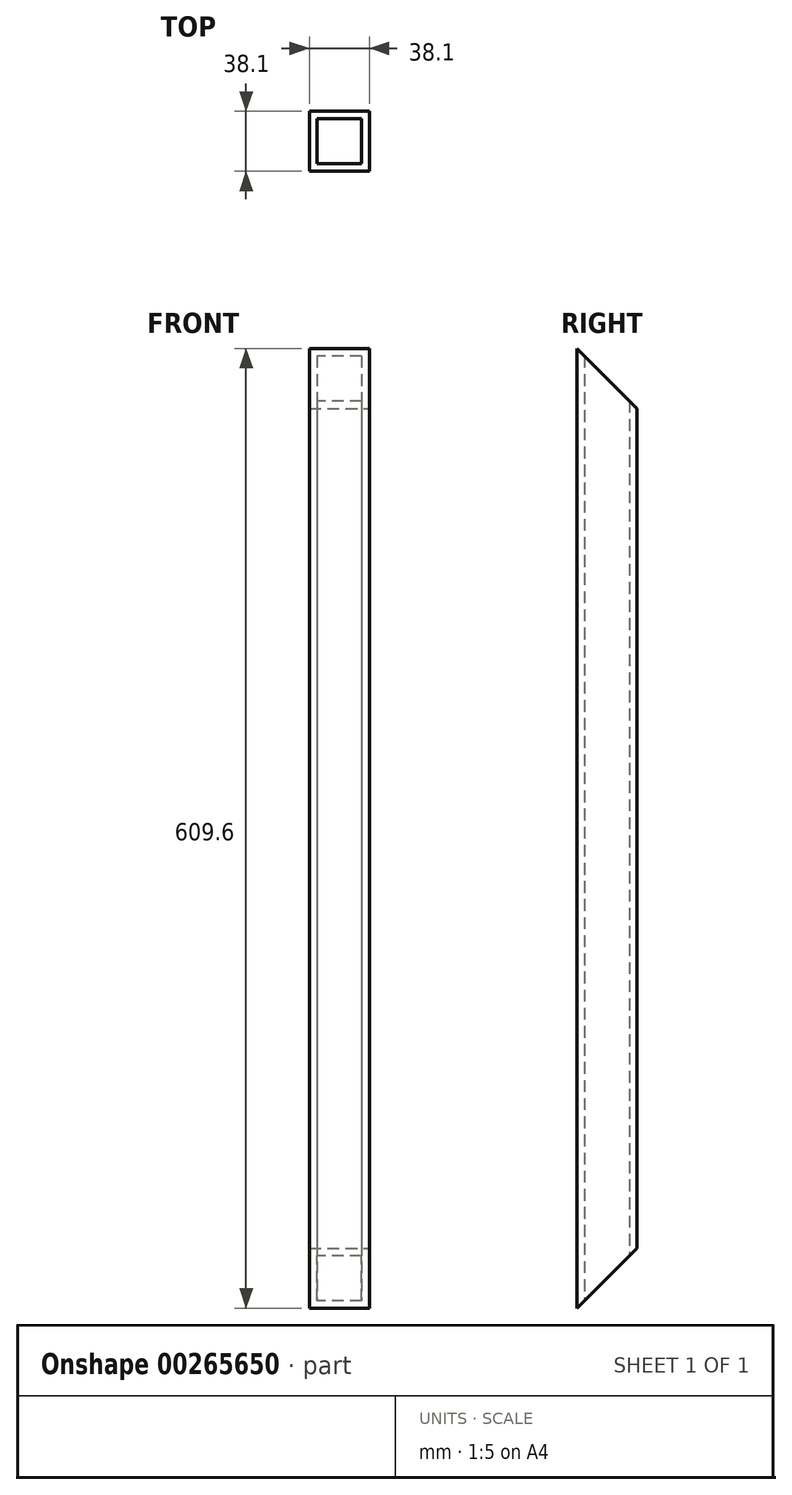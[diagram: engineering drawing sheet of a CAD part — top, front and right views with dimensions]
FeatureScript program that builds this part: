
annotation { "Feature Type Name" : "Feature", "Feature Type Description" : "" }
export const myFeature = defineFeature(function(context is Context, id is Id, definition is map)
    precondition{}
    {
        {
            var Q0;
            Q0=qCreatedBy(makeId("Top.planeOp"),FACE);
            var sketch = newSketch(context, id + "F0", { "sketchPlane" : qUnion([Q0])});
            skLineSegment(sketch, "E0.bottom", {"start": v(-19.05, 19.05) * mm, "end": v(19.05, 19.05) * mm});
            skLineSegment(sketch, "E0.top", {"start": v(-19.05, -19.05) * mm, "end": v(19.05, -19.05) * mm});
            skLineSegment(sketch, "E0.left", {"start": v(-19.05, 19.05) * mm, "end": v(-19.05, -19.05) * mm});
            skLineSegment(sketch, "E0.right", {"start": v(19.05, 19.05) * mm, "end": v(19.05, -19.05) * mm});
            skLineSegment(sketch, "E1.0", {"start": v(-14.27, 14.27) * mm, "end": v(14.27, 14.27) * mm});
            skLineSegment(sketch, "E1.1", {"start": v(-14.27, 14.27) * mm, "end": v(-14.27, -14.27) * mm});
            skLineSegment(sketch, "E1.2", {"start": v(-14.27, -14.27) * mm, "end": v(14.27, -14.27) * mm});
            skLineSegment(sketch, "E1.3", {"start": v(14.27, 14.27) * mm, "end": v(14.27, -14.27) * mm});
            skSolve(sketch);
        }
        {
            var Q0;
            Q0 = qSketchRegion(id + "F0", true);
            extrude(context, id + "F1", {"entities" : qUnion([Q0]), "depth" : 609.6 * mm});
        }
        {
            var Q0;
            Q0=makeQuery(id+"F1.opExtrude","SWEPT_FACE",FACE,{"disambiguationData":[OSD([sQuery(id+"F0.wireOp",EDGE,"E0.right")])]});
            var sketch = newSketch(context, id + "F2", { "sketchPlane" : qUnion([Q0])});
            skLineSegment(sketch, "E2", {"start": v(-19.05, 609.6) * mm, "end": v(19.05, 571.5) * mm});
            skLineSegment(sketch, "E3", {"start": v(-19.05, 0) * mm, "end": v(19.05, 38.1) * mm});
            skSolve(sketch);
        }
        {
            var Q0;
            {var subQ0=sQuery(id+"F2.wireOp",EDGE,"E3");Q0=makeQuery(id+"F2.imprint","IMPRINT",FACE,{"disambiguationData":[TD([[makeQuery(id+"F2.imprint","IMPRINT",EDGE,{"derivedFrom":subQ0}),-1.0]])]});}
            extrude(context, id + "F3", {"entities" : qUnion([Q0]), "operationType" : NewBodyOperationType.REMOVE, "endBound" : BoundingType.THROUGH_ALL, "oppositeDirection" : true, "depth" : 25.4 * mm});
        }
        {
            var Q0;
            {var subQ0=sQuery(id+"F2.wireOp",EDGE,"E2");Q0=makeQuery(id+"F2.imprint","IMPRINT",FACE,{"disambiguationData":[TD([[makeQuery(id+"F2.imprint","IMPRINT",EDGE,{"derivedFrom":subQ0}),1.0]])]});}
            extrude(context, id + "F4", {"entities" : qUnion([Q0]), "operationType" : NewBodyOperationType.REMOVE, "endBound" : BoundingType.THROUGH_ALL, "oppositeDirection" : true, "depth" : 25.4 * mm});
        }
    });
